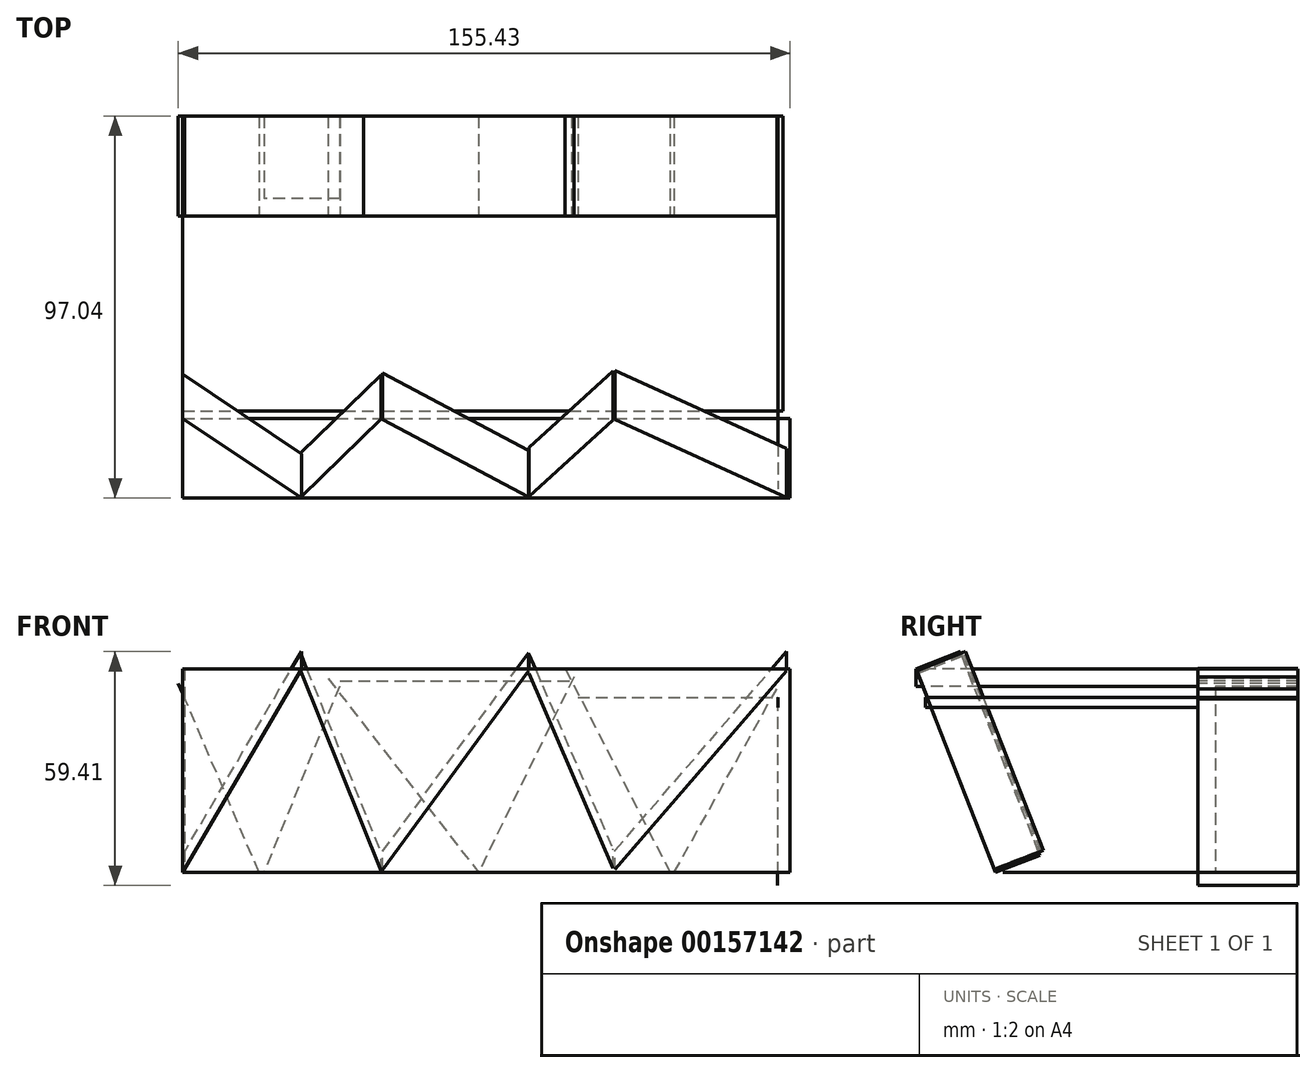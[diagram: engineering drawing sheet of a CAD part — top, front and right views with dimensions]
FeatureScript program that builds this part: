
annotation { "Feature Type Name" : "Feature", "Feature Type Description" : "" }
export const myFeature = defineFeature(function(context is Context, id is Id, definition is map)
    precondition{}
    {
        {
            var Q0;
            Q0=qCreatedBy(makeId("Front.planeOp"),FACE);
            var sketch = newSketch(context, id + "F0", { "sketchPlane" : qUnion([Q0])});
            skLineSegment(sketch, "E0", {"start": v(-76.47, 0) * mm, "end": v(-76.47, 49.29) * mm});
            skLineSegment(sketch, "E1", {"start": v(-76.47, 49.29) * mm, "end": v(76.2, 49.29) * mm});
            skLineSegment(sketch, "E2", {"start": v(76.2, 49.29) * mm, "end": v(76.2, 0) * mm});
            skLineSegment(sketch, "E3", {"start": v(-76.47, 0) * mm, "end": v(-38.21, 49.29) * mm});
            skLineSegment(sketch, "E4", {"start": v(-38.21, 49.29) * mm, "end": v(0, 0) * mm});
            skLineSegment(sketch, "E5", {"start": v(0, 0) * mm, "end": v(35.1, 49.29) * mm});
            skLineSegment(sketch, "E6", {"start": v(35.1, 49.29) * mm, "end": v(76.2, 0) * mm});
            skSolve(sketch);
        }
        {
            var Q0;
            Q0=sQuery(id+"F0.wireOp",EDGE,"E4");
            extrude(context, id + "F1", {"bodyType" : ToolBodyType.SURFACE, "surfaceEntities" : qUnion([Q0]), "depth" : 25.4 * mm});
        }
        {
            var Q0;
            Q0=qCreatedBy(makeId("Front.planeOp"),FACE);
            var sketch = newSketch(context, id + "F2", { "sketchPlane" : qUnion([Q0])});
            skLineSegment(sketch, "E7", {"start": v(-35.33, 47.32) * mm, "end": v(-54.51, 0) * mm});
            skSolve(sketch);
        }
        {
            var Q0;
            Q0=sQuery(id+"F2.wireOp",EDGE,"E7");
            extrude(context, id + "F3", {"bodyType" : ToolBodyType.SURFACE, "surfaceEntities" : qUnion([Q0]), "depth" : 20.95 * mm});
        }
        {
            var Q0;
            Q0=qCreatedBy(makeId("Front.planeOp"),FACE);
            var sketch = newSketch(context, id + "F4", { "sketchPlane" : qUnion([Q0])});
            skLineSegment(sketch, "E8", {"start": v(-35.13, 48.6) * mm, "end": v(23.65, 48.6) * mm});
            skSolve(sketch);
        }
        {
            var Q0;
            Q0=sQuery(id+"F4.wireOp",EDGE,"E8");
            extrude(context, id + "F5", {"bodyType" : ToolBodyType.SURFACE, "surfaceEntities" : qUnion([Q0]), "depth" : 25.4 * mm});
        }
        {
            var Q0;
            Q0=qCreatedBy(makeId("Front.planeOp"),FACE);
            var sketch = newSketch(context, id + "F6", { "sketchPlane" : qUnion([Q0])});
            skLineSegment(sketch, "E9", {"start": v(24.2, 49.63) * mm, "end": v(0, 0) * mm});
            skSolve(sketch);
        }
        {
            var Q0;
            Q0=sQuery(id+"F6.wireOp",EDGE,"E9");
            extrude(context, id + "F7", {"bodyType" : ToolBodyType.SURFACE, "surfaceEntities" : qUnion([Q0]), "depth" : 25.4 * mm});
        }
        {
            var Q0;
            Q0=qCreatedBy(makeId("Front.planeOp"),FACE);
            var sketch = newSketch(context, id + "F8", { "sketchPlane" : qUnion([Q0])});
            skLineSegment(sketch, "E10", {"start": v(22.03, 51.76) * mm, "end": v(48.68, 0) * mm});
            skSolve(sketch);
        }
        {
            var Q0;
            Q0=sQuery(id+"F8.wireOp",EDGE,"E10");
            extrude(context, id + "F9", {"bodyType" : ToolBodyType.SURFACE, "surfaceEntities" : qUnion([Q0]), "depth" : 25.4 * mm});
        }
        {
            var Q0;
            Q0=qCreatedBy(makeId("Front.planeOp"),FACE);
            var sketch = newSketch(context, id + "F10", { "sketchPlane" : qUnion([Q0])});
            skLineSegment(sketch, "E11", {"start": v(-55.76, 0) * mm, "end": v(-76.3, 48.08) * mm});
            skSolve(sketch);
        }
        {
            var Q0;
            Q0=sQuery(id+"F10.wireOp",EDGE,"E11");
            extrude(context, id + "F11", {"bodyType" : ToolBodyType.SURFACE, "surfaceEntities" : qUnion([Q0]), "depth" : 25.4 * mm});
        }
        {
            var Q0;
            Q0=qCreatedBy(makeId("Front.planeOp"),FACE);
            var sketch = newSketch(context, id + "F12", { "sketchPlane" : qUnion([Q0])});
            skLineSegment(sketch, "E12", {"start": v(-75.17, 51.72) * mm, "end": v(-29.23, 51.72) * mm});
            skSolve(sketch);
        }
        {
            var Q0;
            Q0=sQuery(id+"F12.wireOp",EDGE,"E12");
            extrude(context, id + "F13", {"bodyType" : ToolBodyType.SURFACE, "surfaceEntities" : qUnion([Q0]), "depth" : 25.4 * mm});
        }
        {
            var Q0;
            Q0=qCreatedBy(makeId("Front.planeOp"),FACE);
            var sketch = newSketch(context, id + "F14", { "sketchPlane" : qUnion([Q0])});
            skLineSegment(sketch, "E13", {"start": v(25.22, 44.45) * mm, "end": v(76.06, 44.45) * mm});
            skSolve(sketch);
        }
        {
            var Q0;
            Q0=sQuery(id+"F14.wireOp",EDGE,"E13");
            extrude(context, id + "F15", {"bodyType" : ToolBodyType.SURFACE, "surfaceEntities" : qUnion([Q0]), "depth" : 25.4 * mm});
        }
        {
            var Q0;
            Q0=qCreatedBy(makeId("Front.planeOp"),FACE);
            var sketch = newSketch(context, id + "F16", { "sketchPlane" : qUnion([Q0])});
            skLineSegment(sketch, "E14", {"start": v(75.92, 44.1) * mm, "end": v(75.92, -3.29) * mm});
            skSolve(sketch);
        }
        {
            var Q0;
            Q0=sQuery(id+"F16.wireOp",EDGE,"E14");
            extrude(context, id + "F17", {"bodyType" : ToolBodyType.SURFACE, "surfaceEntities" : qUnion([Q0]), "depth" : 25.4 * mm});
        }
        {
            var Q0;
            Q0=qCreatedBy(makeId("Front.planeOp"),FACE);
            var sketch = newSketch(context, id + "F18", { "sketchPlane" : qUnion([Q0])});
            skLineSegment(sketch, "E15", {"start": v(49.68, 0) * mm, "end": v(75.76, 46.63) * mm});
            skSolve(sketch);
        }
        {
            var Q0;
            Q0=sQuery(id+"F18.wireOp",EDGE,"E15");
            extrude(context, id + "F19", {"bodyType" : ToolBodyType.SURFACE, "surfaceEntities" : qUnion([Q0]), "depth" : 25.4 * mm});
        }
        {
            var Q0;
            Q0=qCreatedBy(makeId("Front.planeOp"),FACE);
            var sketch = newSketch(context, id + "F20", { "sketchPlane" : qUnion([Q0])});
            skLineSegment(sketch, "E16", {"start": v(-74.72, 51.8) * mm, "end": v(-74.72, 0) * mm});
            skSolve(sketch);
        }
        {
            var Q0;
            Q0=sQuery(id+"F20.wireOp",EDGE,"E16");
            extrude(context, id + "F21", {"bodyType" : ToolBodyType.SURFACE, "surfaceEntities" : qUnion([Q0]), "depth" : 25.4 * mm});
        }
        {
            var Q0;
            Q0=qCreatedBy(makeId("Front.planeOp"),FACE);
            var sketch = newSketch(context, id + "F22", { "sketchPlane" : qUnion([Q0])});
            skLineSegment(sketch, "E17", {"start": v(-75.19, 0) * mm, "end": v(77.28, 0) * mm});
            skSolve(sketch);
        }
        {
            var Q0;
            Q0=sQuery(id+"F22.wireOp",EDGE,"E17");
            extrude(context, id + "F23", {"bodyType" : ToolBodyType.SURFACE, "surfaceEntities" : qUnion([Q0]), "depth" : 74.93 * mm});
        }
        {
            var Q0;
            Q0=makeQuery(id+"F15.opExtrude","SWEPT_FACE",FACE,{"disambiguationData":[OSD([sQuery(id+"F14.wireOp",EDGE,"E13")])]});
            var sketch = newSketch(context, id + "F24", { "sketchPlane" : qUnion([Q0])});
            skLineSegment(sketch, "E18", {"start": v(76.06, 25.4) * mm, "end": v(76.06, 94.7) * mm});
            skSolve(sketch);
        }
        {
            var Q0;
            Q0=sQuery(id+"F24.wireOp",EDGE,"E18");
            extrude(context, id + "F25", {"bodyType" : ToolBodyType.SURFACE, "surfaceEntities" : qUnion([Q0]), "depth" : 2.54 * mm});
        }
        {
            var Q0;
            Q0=makeQuery(id+"F13.opExtrude","SWEPT_FACE",FACE,{"disambiguationData":[OSD([sQuery(id+"F12.wireOp",EDGE,"E12")])]});
            var sketch = newSketch(context, id + "F26", { "sketchPlane" : qUnion([Q0])});
            skLineSegment(sketch, "E19", {"start": v(-75.17, 25.4) * mm, "end": v(-75.17, 97.04) * mm});
            skSolve(sketch);
        }
        {
            var Q0;
            Q0=sQuery(id+"F26.wireOp",EDGE,"E19");
            extrude(context, id + "F27", {"bodyType" : ToolBodyType.SURFACE, "surfaceEntities" : qUnion([Q0]), "depth" : 4.44 * mm});
        }
        {
            var Q0;
            Q0=makeQuery(id+"F27.opExtrude","SWEPT_FACE",FACE,{"disambiguationData":[OSD([sQuery(id+"F26.wireOp",EDGE,"E19")])]});
            var sketch = newSketch(context, id + "F28", { "sketchPlane" : qUnion([Q0])});
            skLineSegment(sketch, "E20", {"start": v(0, 0) * mm, "end": v(-69.56, 0) * mm});
            skLineSegment(sketch, "E21", {"start": v(-97.04, 51.72) * mm, "end": v(-76.8, 0) * mm});
            skSolve(sketch);
        }
        {
            var Q0;
            Q0=sQuery(id+"F28.wireOp",EDGE,"E21");
            extrude(context, id + "F29", {"bodyType" : ToolBodyType.SURFACE, "surfaceEntities" : qUnion([Q0]), "depth" : 154.3 * mm});
        }
        {
            var Q0;
            Q0=makeQuery(id+"F29.opExtrude","SWEPT_FACE",FACE,{"disambiguationData":[OSD([sQuery(id+"F28.wireOp",EDGE,"E21")])]});
            var sketch = newSketch(context, id + "F30", { "sketchPlane" : qUnion([Q0])});
            skLineSegment(sketch, "E22", {"start": v(-75.17, 28) * mm, "end": v(-45.02, 83.54) * mm});
            skSolve(sketch);
        }
        {
            var Q0;
            {var subQ0=sQuery(id+"F30.wireOp",EDGE,"E22");Q0=makeQuery(id+"F30.imprint","IMPRINT",FACE,{"disambiguationData":[TD([[makeQuery(id+"F30.imprint","IMPRINT",EDGE,{"derivedFrom":subQ0}),-1.0]])]});}
            var sketch = newSketch(context, id + "F31", { "sketchPlane" : qUnion([Q0])});
            skLineSegment(sketch, "E23", {"start": v(-45.09, 82.7) * mm, "end": v(-24.74, 28.48) * mm});
            skSolve(sketch);
        }
        {
            var Q0;
            {var subQ0=sQuery(id+"F30.wireOp",EDGE,"E22");Q0=makeQuery(id+"F30.imprint","IMPRINT",FACE,{"disambiguationData":[TD([[makeQuery(id+"F30.imprint","IMPRINT",EDGE,{"derivedFrom":subQ0}),-1.0]])]});}
            var sketch = newSketch(context, id + "F32", { "sketchPlane" : qUnion([Q0])});
            skLineSegment(sketch, "E24", {"start": v(-24.35, 28.73) * mm, "end": v(12.66, 82.92) * mm});
            skSolve(sketch);
        }
        {
            var Q0;
            {var subQ0=sQuery(id+"F30.wireOp",EDGE,"E22");Q0=makeQuery(id+"F30.imprint","IMPRINT",FACE,{"disambiguationData":[TD([[makeQuery(id+"F30.imprint","IMPRINT",EDGE,{"derivedFrom":subQ0}),-1.0]])]});}
            var sketch = newSketch(context, id + "F33", { "sketchPlane" : qUnion([Q0])});
            skLineSegment(sketch, "E25", {"start": v(12.87, 82.3) * mm, "end": v(34.13, 29.16) * mm});
            skSolve(sketch);
        }
        {
            var Q0;
            {var subQ0=sQuery(id+"F30.wireOp",EDGE,"E22");Q0=makeQuery(id+"F30.imprint","IMPRINT",FACE,{"disambiguationData":[TD([[makeQuery(id+"F30.imprint","IMPRINT",EDGE,{"derivedFrom":subQ0}),-1.0]])]});}
            var sketch = newSketch(context, id + "F34", { "sketchPlane" : qUnion([Q0])});
            skLineSegment(sketch, "E26", {"start": v(34.73, 28.78) * mm, "end": v(78.24, 83.01) * mm});
            skSolve(sketch);
        }
        {
            var Q0;
            Q0=sQuery(id+"F30.wireOp",EDGE,"E22");
            var Q1;
            Q1=sQuery(id+"F31.wireOp",EDGE,"E23");
            extrude(context, id + "F35", {"bodyType" : ToolBodyType.SURFACE, "surfaceEntities" : qUnion([Q0, Q1]), "oppositeDirection" : true, "depth" : 12.06 * mm});
        }
        {
            var Q0;
            Q0=sQuery(id+"F32.wireOp",EDGE,"E24");
            extrude(context, id + "F36", {"bodyType" : ToolBodyType.SURFACE, "surfaceEntities" : qUnion([Q0]), "oppositeDirection" : true, "depth" : 12.7 * mm});
        }
        {
            var Q0;
            Q0=sQuery(id+"F33.wireOp",EDGE,"E25");
            var Q1;
            Q1=sQuery(id+"F34.wireOp",EDGE,"E26");
            extrude(context, id + "F37", {"bodyType" : ToolBodyType.SURFACE, "surfaceEntities" : qUnion([Q0, Q1]), "oppositeDirection" : true, "depth" : 13.33 * mm});
        }
    });
